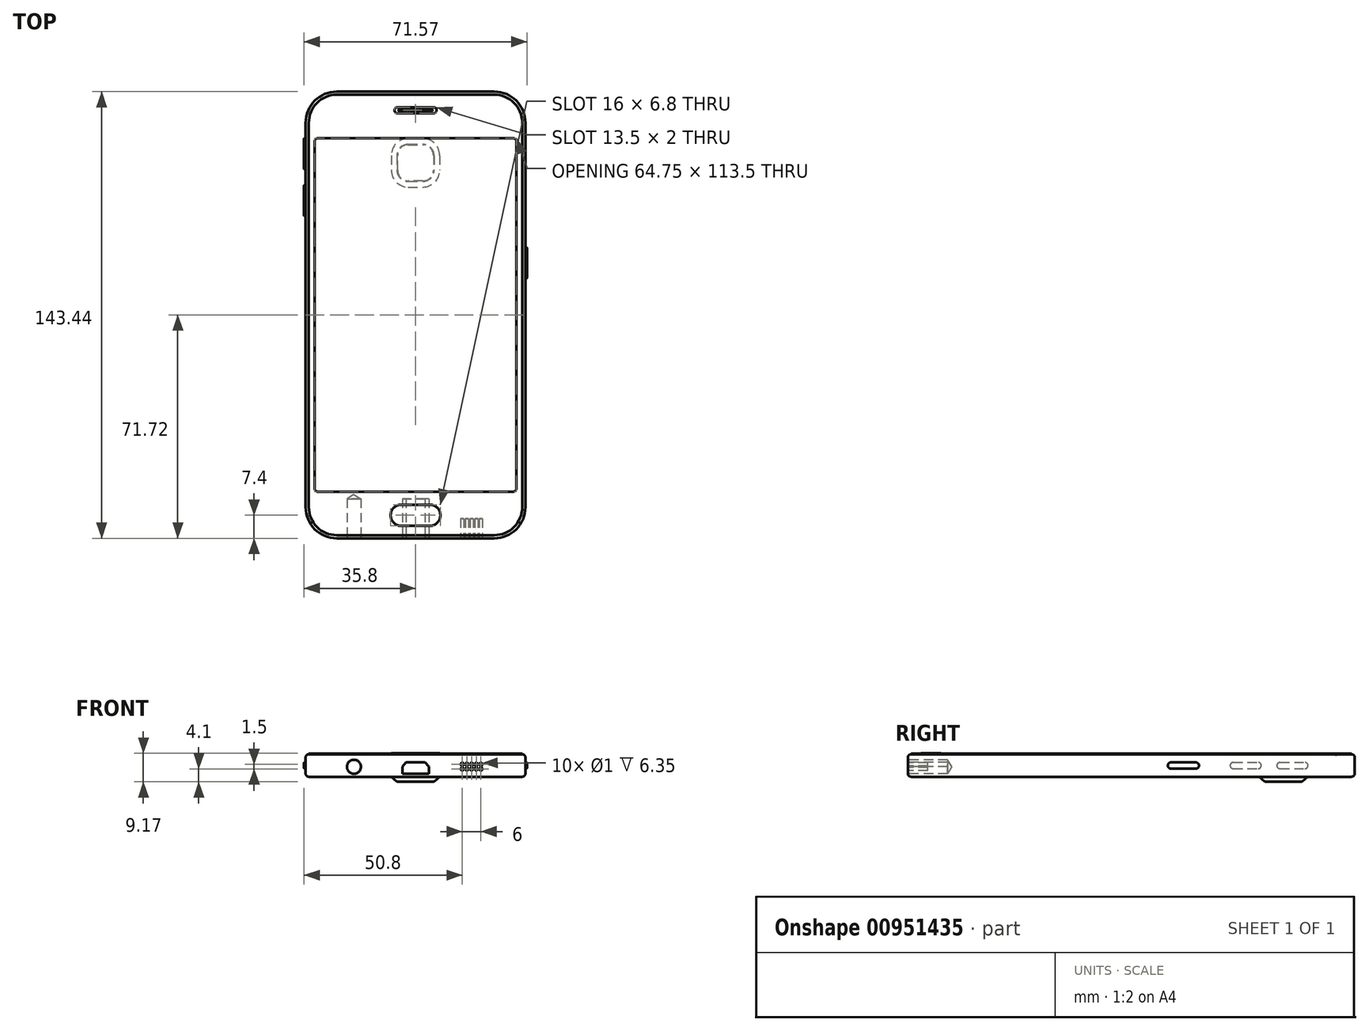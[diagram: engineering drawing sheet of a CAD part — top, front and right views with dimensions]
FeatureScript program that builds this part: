
annotation { "Feature Type Name" : "Feature", "Feature Type Description" : "" }
export const myFeature = defineFeature(function(context is Context, id is Id, definition is map)
    precondition{}
    {
        {
            var Q0;
            Q0=qCreatedBy(makeId("Top.planeOp"),FACE);
            var sketch = newSketch(context, id + "F0", { "sketchPlane" : qUnion([Q0])});
            skLineSegment(sketch, "E0.bottom", {"start": v(-35.27, 71.72) * mm, "end": v(35.27, 71.72) * mm});
            skLineSegment(sketch, "E0.top", {"start": v(-35.27, -71.72) * mm, "end": v(35.27, -71.72) * mm});
            skLineSegment(sketch, "E0.left", {"start": v(-35.27, 71.72) * mm, "end": v(-35.27, -71.72) * mm});
            skLineSegment(sketch, "E0.right", {"start": v(35.27, 71.72) * mm, "end": v(35.27, -71.72) * mm});
            skLineSegment(sketch, "E1", {"start": v(0, 0) * mm, "end": v(0, -71.72) * mm, "construction": true});
            skLineSegment(sketch, "E2", {"start": v(-35.27, 0) * mm, "end": v(0, 0) * mm, "construction": true});
            skPoint(sketch, "E3.orphan", {"position": v(35.27, 0) * mm});
            skPoint(sketch, "E4.orphan", {"position": v(0, 71.72) * mm});
            skSolve(sketch);
        }
        {
            var Q0;
            Q0=makeQuery(id+"F0.imprint","IMPRINT",FACE,{"disambiguationData":[TD([[makeQuery(id+"F0.imprint","IMPRINT",EDGE,{"derivedFrom":sQuery(id+"F0.wireOp",EDGE,"E0.bottom")}),-1.0]])]});
            extrude(context, id + "F1", {"entities" : qUnion([Q0]), "depth" : 7.22 * mm});
        }
        {
            var Q0;
            Q0=makeQuery(id+"F1.opExtrude","SWEPT_EDGE",EDGE,{"disambiguationData":[OSD([sQuery(id+"F0.wireOp",EDGE,"E0.bottom"),sQuery(id+"F0.wireOp",EDGE,"E0.left")])]});
            var Q1;
            Q1=makeQuery(id+"F1.opExtrude","SWEPT_EDGE",EDGE,{"disambiguationData":[OSD([sQuery(id+"F0.wireOp",EDGE,"E0.top"),sQuery(id+"F0.wireOp",EDGE,"E0.left")])]});
            var Q2;
            Q2=makeQuery(id+"F1.opExtrude","SWEPT_EDGE",EDGE,{"disambiguationData":[OSD([sQuery(id+"F0.wireOp",EDGE,"E0.top"),sQuery(id+"F0.wireOp",EDGE,"E0.right")])]});
            var Q3;
            Q3=makeQuery(id+"F1.opExtrude","SWEPT_EDGE",EDGE,{"disambiguationData":[OSD([sQuery(id+"F0.wireOp",EDGE,"E0.bottom"),sQuery(id+"F0.wireOp",EDGE,"E0.right")])]});
            fillet(context, id + "F2", {"entities" : qUnion([Q0, Q1, Q2, Q3]), "radius" : 10 * mm, "tangentPropagation" : true, "allowEdgeOverflow" : false});
        }
        {
            var Q0;
            Q0=makeQuery(id+"F1.opExtrude","CAP_FACE",FACE,{"disambiguationData":[OSD([sQuery(id+"F0.wireOp",EDGE,"E0.bottom"),sQuery(id+"F0.wireOp",EDGE,"E0.top"),sQuery(id+"F0.wireOp",EDGE,"E0.left"),sQuery(id+"F0.wireOp",EDGE,"E0.right")])],"isStart":false});
            var sketch = newSketch(context, id + "F3", { "sketchPlane" : qUnion([Q0])});
            skLineSegment(sketch, "E5.bottom", {"start": v(-4.6, -60.92) * mm, "end": v(4.6, -60.92) * mm});
            skLineSegment(sketch, "E5.top", {"start": v(-4.6, -67.72) * mm, "end": v(4.6, -67.72) * mm});
            skLineSegment(sketch, "E5.left", {"start": v(-8, -64.32) * mm, "end": v(-8, -64.32) * mm});
            skLineSegment(sketch, "E5.right", {"start": v(8, -64.32) * mm, "end": v(8, -64.32) * mm});
            skLineSegment(sketch, "E6", {"start": v(-8, -64.32) * mm, "end": v(8, -64.32) * mm, "construction": true});
            skLineSegment(sketch, "E7", {"start": v(0, -60.92) * mm, "end": v(0, -67.72) * mm, "construction": true});
            skPoint(sketch, "E8.visualSharp", {"position": v(-8, -60.92) * mm});
            skArc(sketch, "E8.filletArc", {"start": v(-4.6, -60.92) * mm, "mid": v(-7, -61.92) * mm, "end": v(-8, -64.32) * mm});
            skPoint(sketch, "E9.visualSharp", {"position": v(8, -60.92) * mm});
            skArc(sketch, "E9.filletArc", {"start": v(8, -64.32) * mm, "mid": v(7, -61.92) * mm, "end": v(4.6, -60.92) * mm});
            skPoint(sketch, "E10.visualSharp", {"position": v(8, -67.72) * mm});
            skArc(sketch, "E10.filletArc", {"start": v(4.6, -67.72) * mm, "mid": v(7, -66.72) * mm, "end": v(8, -64.32) * mm});
            skPoint(sketch, "E11.visualSharp", {"position": v(-8, -67.72) * mm});
            skArc(sketch, "E11.filletArc", {"start": v(-8, -64.32) * mm, "mid": v(-7, -66.72) * mm, "end": v(-4.6, -67.72) * mm});
            skSolve(sketch);
        }
        {
            var Q0;
            Q0=makeQuery(id+"F3.imprint","IMPRINT",FACE,{"disambiguationData":[TD([[makeQuery(id+"F3.imprint","IMPRINT",EDGE,{"derivedFrom":sQuery(id+"F3.wireOp",EDGE,"E5.bottom")}),-1.0]])]});
            extrude(context, id + "F4", {"entities" : qUnion([Q0]), "operationType" : NewBodyOperationType.ADD, "depth" : .35 * mm});
        }
        {
            var Q0;
            Q0=makeQuery(id+"F1.opExtrude","CAP_EDGE",EDGE,{"disambiguationData":[OSD([sQuery(id+"F0.wireOp",EDGE,"E0.left")])],"isStart":false});
            var Q1;
            Q1=makeQuery(id+"F1.opExtrude","CAP_EDGE",EDGE,{"disambiguationData":[OSD([sQuery(id+"F0.wireOp",EDGE,"E0.left")])],"isStart":true});
            fillet(context, id + "F5", {"entities" : qUnion([Q0, Q1]), "radius" : 1 * mm, "tangentPropagation" : true, "allowEdgeOverflow" : false});
        }
        {
            var Q0;
            Q0=makeQuery(id+"F1.opExtrude","SWEPT_FACE",FACE,{"disambiguationData":[OSD([sQuery(id+"F0.wireOp",EDGE,"E0.left")])]});
            var sketch = newSketch(context, id + "F6", { "sketchPlane" : qUnion([Q0])});
            skLineSegment(sketch, "E12.bottom", {"start": v(-31.72, 4.61) * mm, "end": v(-41.72, 4.61) * mm});
            skLineSegment(sketch, "E12.top", {"start": v(-31.72, 2.6) * mm, "end": v(-41.72, 2.61) * mm});
            skLineSegment(sketch, "E12.left", {"start": v(-31.72, 4.61) * mm, "end": v(-31.72, 2.6) * mm});
            skLineSegment(sketch, "E12.right", {"start": v(-41.72, 4.61) * mm, "end": v(-41.72, 2.61) * mm});
            skLineSegment(sketch, "E13.bottom", {"start": v(-46.72, 4.61) * mm, "end": v(-56.72, 4.61) * mm});
            skLineSegment(sketch, "E13.top", {"start": v(-46.72, 2.61) * mm, "end": v(-56.72, 2.61) * mm});
            skLineSegment(sketch, "E13.left", {"start": v(-46.72, 4.61) * mm, "end": v(-46.72, 2.61) * mm});
            skLineSegment(sketch, "E13.right", {"start": v(-56.72, 4.61) * mm, "end": v(-56.72, 2.61) * mm});
            skLineSegment(sketch, "E14", {"start": v(-31.72, 3.6) * mm, "end": v(-41.72, 3.6) * mm, "construction": true});
            skLineSegment(sketch, "E15", {"start": v(-36.72, 2.6) * mm, "end": v(-36.72, 4.6) * mm, "construction": true});
            skLineSegment(sketch, "E16", {"start": v(-51.72, 4.6) * mm, "end": v(-51.72, 2.61) * mm, "construction": true});
            skLineSegment(sketch, "E17", {"start": v(-46.72, 3.6) * mm, "end": v(-56.72, 3.6) * mm, "construction": true});
            skSolve(sketch);
        }
        {
            var Q0;
            Q0=qSketchRegion(id+"F6",true);
            extrude(context, id + "F7", {"entities" : qUnion([Q0]), "operationType" : NewBodyOperationType.ADD, "depth" : .53 * mm});
        }
        {
            var Q0;
            Q0=makeQuery(id+"F7.opExtrude","SWEPT_EDGE",EDGE,{"disambiguationData":[OSD([sQuery(id+"F6.wireOp",EDGE,"E13.bottom"),sQuery(id+"F6.wireOp",EDGE,"E13.right")])]});
            var Q1;
            Q1=makeQuery(id+"F7.opExtrude","SWEPT_EDGE",EDGE,{"disambiguationData":[OSD([sQuery(id+"F6.wireOp",EDGE,"E13.top"),sQuery(id+"F6.wireOp",EDGE,"E13.right")])]});
            var Q2;
            Q2=makeQuery(id+"F7.opExtrude","SWEPT_EDGE",EDGE,{"disambiguationData":[OSD([sQuery(id+"F6.wireOp",EDGE,"E13.top"),sQuery(id+"F6.wireOp",EDGE,"E13.left")])]});
            var Q3;
            Q3=makeQuery(id+"F7.opExtrude","SWEPT_EDGE",EDGE,{"disambiguationData":[OSD([sQuery(id+"F6.wireOp",EDGE,"E13.bottom"),sQuery(id+"F6.wireOp",EDGE,"E13.left")])]});
            var Q4;
            Q4=makeQuery(id+"F7.opExtrude","SWEPT_EDGE",EDGE,{"disambiguationData":[OSD([sQuery(id+"F6.wireOp",EDGE,"E12.bottom"),sQuery(id+"F6.wireOp",EDGE,"E12.right")])]});
            var Q5;
            Q5=makeQuery(id+"F7.opExtrude","SWEPT_EDGE",EDGE,{"disambiguationData":[OSD([sQuery(id+"F6.wireOp",EDGE,"E12.top"),sQuery(id+"F6.wireOp",EDGE,"E12.right")])]});
            var Q6;
            Q6=makeQuery(id+"F7.opExtrude","SWEPT_EDGE",EDGE,{"disambiguationData":[OSD([sQuery(id+"F6.wireOp",EDGE,"E12.top"),sQuery(id+"F6.wireOp",EDGE,"E12.left")])]});
            var Q7;
            Q7=makeQuery(id+"F7.opExtrude","SWEPT_EDGE",EDGE,{"disambiguationData":[OSD([sQuery(id+"F6.wireOp",EDGE,"E12.bottom"),sQuery(id+"F6.wireOp",EDGE,"E12.left")])]});
            fillet(context, id + "F8", {"entities" : qUnion([Q0, Q1, Q2, Q3, Q4, Q5, Q6, Q7]), "radius" : 1 * mm, "tangentPropagation" : true, "allowEdgeOverflow" : false});
        }
        {
            var Q0;
            Q0=makeQuery(id+"F7.opExtrude","CAP_EDGE",EDGE,{"disambiguationData":[OSD([sQuery(id+"F6.wireOp",EDGE,"E13.top")])],"isStart":false});
            var Q1;
            Q1=makeQuery(id+"F7.opExtrude","CAP_EDGE",EDGE,{"disambiguationData":[OSD([sQuery(id+"F6.wireOp",EDGE,"E12.top")])],"isStart":false});
            fillet(context, id + "F9", {"entities" : qUnion([Q0, Q1]), "radius" : .25 * mm, "tangentPropagation" : true, "allowEdgeOverflow" : false});
        }
        {
            var Q0;
            Q0=makeQuery(id+"F1.opExtrude","CAP_FACE",FACE,{"disambiguationData":[OSD([sQuery(id+"F0.wireOp",EDGE,"E0.bottom"),sQuery(id+"F0.wireOp",EDGE,"E0.top"),sQuery(id+"F0.wireOp",EDGE,"E0.left"),sQuery(id+"F0.wireOp",EDGE,"E0.right")])],"isStart":true});
            var sketch = newSketch(context, id + "F10", { "sketchPlane" : qUnion([Q0])});
            skLineSegment(sketch, "E18.bottom", {"start": v(7.88, -40.97) * mm, "end": v(-7.87, -40.97) * mm});
            skLineSegment(sketch, "E18.top", {"start": v(7.88, -56.72) * mm, "end": v(-7.87, -56.72) * mm});
            skLineSegment(sketch, "E18.left", {"start": v(7.88, -40.97) * mm, "end": v(7.88, -56.72) * mm});
            skLineSegment(sketch, "E18.right", {"start": v(-7.87, -40.97) * mm, "end": v(-7.87, -56.72) * mm});
            skLineSegment(sketch, "E19", {"start": v(0, -40.97) * mm, "end": v(0, -56.72) * mm, "construction": true});
            skLineSegment(sketch, "E20", {"start": v(-7.87, -48.84) * mm, "end": v(7.88, -48.84) * mm, "construction": true});
            skSolve(sketch);
        }
        {
            var Q0;
            Q0=qSketchRegion(id+"F10",true);
            extrude(context, id + "F11", {"entities" : qUnion([Q0]), "operationType" : NewBodyOperationType.ADD, "depth" : 1.6 * mm});
        }
        {
            var Q0;
            Q0=makeQuery(id+"F11.opExtrude","SWEPT_EDGE",EDGE,{"disambiguationData":[OSD([sQuery(id+"F10.wireOp",EDGE,"E18.bottom"),sQuery(id+"F10.wireOp",EDGE,"E18.right")])]});
            var Q1;
            Q1=makeQuery(id+"F11.opExtrude","SWEPT_EDGE",EDGE,{"disambiguationData":[OSD([sQuery(id+"F10.wireOp",EDGE,"E18.top"),sQuery(id+"F10.wireOp",EDGE,"E18.right")])]});
            var Q2;
            Q2=makeQuery(id+"F11.opExtrude","SWEPT_EDGE",EDGE,{"disambiguationData":[OSD([sQuery(id+"F10.wireOp",EDGE,"E18.top"),sQuery(id+"F10.wireOp",EDGE,"E18.left")])]});
            var Q3;
            Q3=makeQuery(id+"F11.opExtrude","SWEPT_EDGE",EDGE,{"disambiguationData":[OSD([sQuery(id+"F10.wireOp",EDGE,"E18.bottom"),sQuery(id+"F10.wireOp",EDGE,"E18.left")])]});
            fillet(context, id + "F12", {"entities" : qUnion([Q0, Q1, Q2, Q3]), "radius" : 5.5 * mm, "tangentPropagation" : true, "allowEdgeOverflow" : false});
        }
        {
            var Q0;
            Q0=makeQuery(id+"F11.opExtrude","CAP_EDGE",EDGE,{"disambiguationData":[OSD([sQuery(id+"F10.wireOp",EDGE,"E18.right")])],"isStart":false});
            chamfer(context, id + "F13", {"entities" : qUnion([Q0]), "chamferType" : ChamferType.OFFSET_ANGLE, "width" : 2 * mm, "oppositeDirection" : false, "angle" : 40 * degree, "tangentPropagation" : true});
        }
        {
            var Q0;
            {var subQ0=sQuery(id+"F10.wireOp",EDGE,"E18.right");var subQ1=sQuery(id+"F10.wireOp",EDGE,"E18.top");var subQ2=makeQuery(id+"F11.opExtrude","CAP_FACE",FACE,{"disambiguationData":[OSD([sQuery(id+"F10.wireOp",EDGE,"E18.bottom"),subQ1,sQuery(id+"F10.wireOp",EDGE,"E18.left"),subQ0])],"isStart":false});Q0=makeQuery(id+"F13.opChamfer","BLEND_EDGE",EDGE,{"blendedFrom":[makeQuery(id+"F12.opFillet","BLEND_EDGE",EDGE,{"blendedFrom":[makeQuery(id+"F11.opExtrude","SWEPT_EDGE",EDGE,{"disambiguationData":[OSD([subQ1,subQ0])]}),subQ2],"blendedInto":[subQ2]}),subQ2],"blendedInto":[subQ2]});}
            chamfer(context, id + "F14", {"entities" : qUnion([Q0]), "width" : .25 * mm, "tangentPropagation" : true});
        }
        {
            var Q0;
            Q0=makeQuery(id+"F4.opExtrude","CAP_EDGE",EDGE,{"disambiguationData":[OSD([sQuery(id+"F3.wireOp",EDGE,"E5.top")])],"isStart":false});
            fillet(context, id + "F15", {"entities" : qUnion([Q0]), "radius" : .5 * mm, "tangentPropagation" : true, "allowEdgeOverflow" : false});
        }
        {
            var Q0;
            Q0=makeQuery(id+"F1.opExtrude","SWEPT_FACE",FACE,{"disambiguationData":[OSD([sQuery(id+"F0.wireOp",EDGE,"E0.right")])]});
            var sketch = newSketch(context, id + "F16", { "sketchPlane" : qUnion([Q0])});
            skLineSegment(sketch, "E21.bottom", {"start": v(11.72, 4.61) * mm, "end": v(21.72, 4.61) * mm});
            skLineSegment(sketch, "E21.top", {"start": v(11.72, 2.61) * mm, "end": v(21.72, 2.61) * mm});
            skLineSegment(sketch, "E21.left", {"start": v(11.72, 4.61) * mm, "end": v(11.72, 2.61) * mm});
            skLineSegment(sketch, "E21.right", {"start": v(21.72, 4.61) * mm, "end": v(21.72, 2.61) * mm});
            skLineSegment(sketch, "E22", {"start": v(11.72, 3.6) * mm, "end": v(21.72, 3.6) * mm, "construction": true});
            skLineSegment(sketch, "E23", {"start": v(16.72, 2.61) * mm, "end": v(16.72, 4.61) * mm, "construction": true});
            skSolve(sketch);
        }
        {
            var Q0;
            Q0=makeQuery(id+"F16.imprint","IMPRINT",FACE,{"disambiguationData":[TD([[makeQuery(id+"F16.imprint","IMPRINT",EDGE,{"derivedFrom":sQuery(id+"F16.wireOp",EDGE,"E21.bottom")}),-1.0]])]});
            extrude(context, id + "F17", {"entities" : qUnion([Q0]), "operationType" : NewBodyOperationType.ADD, "depth" : .5 * mm});
        }
        {
            var Q0;
            Q0=makeQuery(id+"F17.opExtrude","SWEPT_EDGE",EDGE,{"disambiguationData":[OSD([sQuery(id+"F16.wireOp",EDGE,"E21.bottom"),sQuery(id+"F16.wireOp",EDGE,"E21.left")])]});
            var Q1;
            Q1=makeQuery(id+"F17.opExtrude","SWEPT_EDGE",EDGE,{"disambiguationData":[OSD([sQuery(id+"F16.wireOp",EDGE,"E21.top"),sQuery(id+"F16.wireOp",EDGE,"E21.left")])]});
            var Q2;
            Q2=makeQuery(id+"F17.opExtrude","SWEPT_EDGE",EDGE,{"disambiguationData":[OSD([sQuery(id+"F16.wireOp",EDGE,"E21.top"),sQuery(id+"F16.wireOp",EDGE,"E21.right")])]});
            var Q3;
            Q3=makeQuery(id+"F17.opExtrude","SWEPT_EDGE",EDGE,{"disambiguationData":[OSD([sQuery(id+"F16.wireOp",EDGE,"E21.bottom"),sQuery(id+"F16.wireOp",EDGE,"E21.right")])]});
            fillet(context, id + "F18", {"entities" : qUnion([Q0, Q1, Q2, Q3]), "radius" : 1 * mm, "tangentPropagation" : true, "allowEdgeOverflow" : false});
        }
        {
            var Q0;
            Q0=makeQuery(id+"F17.opExtrude","CAP_EDGE",EDGE,{"disambiguationData":[OSD([sQuery(id+"F16.wireOp",EDGE,"E21.bottom")])],"isStart":false});
            fillet(context, id + "F19", {"entities" : qUnion([Q0]), "radius" : .25 * mm, "tangentPropagation" : true, "allowEdgeOverflow" : false});
        }
        {
            var Q0;
            Q0=makeQuery(id+"F1.opExtrude","SWEPT_FACE",FACE,{"disambiguationData":[OSD([sQuery(id+"F0.wireOp",EDGE,"E0.top")])]});
            var sketch = newSketch(context, id + "F20", { "sketchPlane" : qUnion([Q0])});
            skCircle(sketch, "E24", {"center": v(-19.77, 3.2) * mm, "radius": 2.25 * mm});
            skSolve(sketch);
        }
        {
            var Q0;
            Q0=sQuery(id+"F20.wireOp",VERTEX,"E24.center");
            var Q1;
            Q1=makeQuery(id+"F1.opExtrude","SWEPT_BODY",BODY,{"disambiguationData":[OSD([sQuery(id+"F0.wireOp",EDGE,"E0.bottom"),sQuery(id+"F0.wireOp",EDGE,"E0.top"),sQuery(id+"F0.wireOp",EDGE,"E0.left"),sQuery(id+"F0.wireOp",EDGE,"E0.right")])]});
            hole(context, id + "F21", {"style" : HoleStyle.SIMPLE, "endStyle" : HoleEndStyle.BLIND, "holeDiameter" : 4.5 * mm, "holeDepth" : 12.7 * mm, "tappedDepth" : 12.7 * mm, "tapClearance" : 3, "locations" : qUnion([Q0]), "scope" : qUnion([Q1])});
        }
        {
            var Q0;
            Q0=makeQuery(id+"F1.opExtrude","SWEPT_FACE",FACE,{"disambiguationData":[OSD([sQuery(id+"F0.wireOp",EDGE,"E0.top")])]});
            var sketch = newSketch(context, id + "F22", { "sketchPlane" : qUnion([Q0])});
            skLineSegment(sketch, "E25", {"start": v(-4.25, 3.3) * mm, "end": v(-4.25, 1) * mm});
            skLineSegment(sketch, "E26", {"start": v(-4.25, 1) * mm, "end": v(4.25, 1) * mm});
            skLineSegment(sketch, "E27", {"start": v(4.25, 1) * mm, "end": v(4.25, 3.3) * mm});
            skLineSegment(sketch, "E28", {"start": v(4.25, 3.3) * mm, "end": v(3, 4.6) * mm});
            skLineSegment(sketch, "E29", {"start": v(3, 4.6) * mm, "end": v(-3, 4.6) * mm});
            skLineSegment(sketch, "E30", {"start": v(-3, 4.6) * mm, "end": v(-4.25, 3.3) * mm});
            skLineSegment(sketch, "E31", {"start": v(0, 4.6) * mm, "end": v(0, 1) * mm, "construction": true});
            skSolve(sketch);
        }
        {
            var Q0;
            Q0=makeQuery(id+"F22.imprint","IMPRINT",FACE,{"disambiguationData":[TD([[makeQuery(id+"F22.imprint","IMPRINT",EDGE,{"derivedFrom":sQuery(id+"F22.wireOp",EDGE,"E25")}),1.0]])]});
            extrude(context, id + "F23", {"entities" : qUnion([Q0]), "operationType" : NewBodyOperationType.REMOVE, "oppositeDirection" : true, "depth" : 12.7 * mm});
        }
        {
            var Q0;
            Q0=makeQuery(id+"F1.opExtrude","SWEPT_FACE",FACE,{"disambiguationData":[OSD([sQuery(id+"F0.wireOp",EDGE,"E0.top")])]});
            var sketch = newSketch(context, id + "F24", { "sketchPlane" : qUnion([Q0])});
            skCircle(sketch, "E32", {"center": v(15, 2.5) * mm, "radius": 0.5 * mm});
            skCircle(sketch, "E33.0.1.0", {"center": v(15, 4) * mm, "radius": 0.5 * mm});
            skCircle(sketch, "E33.1.0.0", {"center": v(16.5, 2.5) * mm, "radius": 0.5 * mm});
            skCircle(sketch, "E33.1.1.0", {"center": v(16.5, 4) * mm, "radius": 0.5 * mm});
            skCircle(sketch, "E33.2.0.0", {"center": v(18, 2.5) * mm, "radius": 0.5 * mm});
            skCircle(sketch, "E33.2.1.0", {"center": v(18, 4) * mm, "radius": 0.5 * mm});
            skCircle(sketch, "E33.3.0.0", {"center": v(19.5, 2.5) * mm, "radius": 0.5 * mm});
            skCircle(sketch, "E33.3.1.0", {"center": v(19.5, 4) * mm, "radius": 0.5 * mm});
            skCircle(sketch, "E33.4.0.0", {"center": v(21, 2.5) * mm, "radius": 0.5 * mm});
            skCircle(sketch, "E33.4.1.0", {"center": v(21, 4) * mm, "radius": 0.5 * mm});
            skLineSegment(sketch, "E33.direction1", {"start": v(15, 2.5) * mm, "end": v(16.5, 2.5) * mm, "construction": true});
            skLineSegment(sketch, "E33.direction2", {"start": v(15, 2.5) * mm, "end": v(15, 4) * mm, "construction": true});
            skSolve(sketch);
        }
        {
            var Q0;
            Q0=qSketchRegion(id+"F24",true);
            extrude(context, id + "F25", {"entities" : qUnion([Q0]), "operationType" : NewBodyOperationType.REMOVE, "oppositeDirection" : true, "depth" : 6.35 * mm});
        }
        {
            var Q0;
            Q0=makeQuery(id+"F1.opExtrude","CAP_FACE",FACE,{"disambiguationData":[OSD([sQuery(id+"F0.wireOp",EDGE,"E0.bottom"),sQuery(id+"F0.wireOp",EDGE,"E0.top"),sQuery(id+"F0.wireOp",EDGE,"E0.left"),sQuery(id+"F0.wireOp",EDGE,"E0.right")])],"isStart":false});
            var sketch = newSketch(context, id + "F26", { "sketchPlane" : qUnion([Q0])});
            skCircle(sketch, "E34", {"center": v(-5.25, 65.72) * mm, "radius": 0.25 * mm});
            skCircle(sketch, "E35.1.0.0", {"center": v(-4.5, 65.72) * mm, "radius": 0.25 * mm});
            skCircle(sketch, "E35.2.0.0", {"center": v(-3.75, 65.72) * mm, "radius": 0.25 * mm});
            skCircle(sketch, "E35.3.0.0", {"center": v(-3, 65.72) * mm, "radius": 0.25 * mm});
            skCircle(sketch, "E35.4.0.0", {"center": v(-2.25, 65.72) * mm, "radius": 0.25 * mm});
            skCircle(sketch, "E35.5.0.0", {"center": v(-1.5, 65.72) * mm, "radius": 0.25 * mm});
            skCircle(sketch, "E35.6.0.0", {"center": v(-0.75, 65.72) * mm, "radius": 0.25 * mm});
            skCircle(sketch, "E35.7.0.0", {"center": v(0, 65.72) * mm, "radius": 0.25 * mm});
            skCircle(sketch, "E35.8.0.0", {"center": v(0.75, 65.72) * mm, "radius": 0.25 * mm});
            skCircle(sketch, "E35.9.0.0", {"center": v(1.5, 65.72) * mm, "radius": 0.25 * mm});
            skCircle(sketch, "E35.10.0.0", {"center": v(2.25, 65.72) * mm, "radius": 0.25 * mm});
            skCircle(sketch, "E35.11.0.0", {"center": v(3, 65.72) * mm, "radius": 0.25 * mm});
            skCircle(sketch, "E35.12.0.0", {"center": v(3.75, 65.72) * mm, "radius": 0.25 * mm});
            skCircle(sketch, "E35.13.0.0", {"center": v(4.5, 65.72) * mm, "radius": 0.25 * mm});
            skCircle(sketch, "E35.14.0.0", {"center": v(5.25, 65.72) * mm, "radius": 0.25 * mm});
            skLineSegment(sketch, "E35.direction1", {"start": v(-5.25, 65.72) * mm, "end": v(-4.5, 65.72) * mm, "construction": true});
            skLineSegment(sketch, "E36", {"start": v(0, 65.72) * mm, "end": v(0, 65.97) * mm, "construction": true});
            skSolve(sketch);
        }
        {
            var Q0;
            Q0=qSketchRegion(id+"F26",true);
            extrude(context, id + "F27", {"entities" : qUnion([Q0]), "operationType" : NewBodyOperationType.REMOVE, "oppositeDirection" : true, "depth" : .25 * mm});
        }
        {
            var Q0;
            Q0=makeQuery(id+"F1.opExtrude","CAP_FACE",FACE,{"disambiguationData":[OSD([sQuery(id+"F0.wireOp",EDGE,"E0.bottom"),sQuery(id+"F0.wireOp",EDGE,"E0.top"),sQuery(id+"F0.wireOp",EDGE,"E0.left"),sQuery(id+"F0.wireOp",EDGE,"E0.right")])],"isStart":false});
            var sketch = newSketch(context, id + "F28", { "sketchPlane" : qUnion([Q0])});
            skLineSegment(sketch, "E37.bottom", {"start": v(-6.75, 66.72) * mm, "end": v(6.75, 66.72) * mm});
            skLineSegment(sketch, "E37.top", {"start": v(-6.75, 64.72) * mm, "end": v(6.75, 64.72) * mm});
            skLineSegment(sketch, "E37.left", {"start": v(-6.75, 66.72) * mm, "end": v(-6.75, 64.72) * mm});
            skLineSegment(sketch, "E37.right", {"start": v(6.75, 66.72) * mm, "end": v(6.75, 64.72) * mm});
            skLineSegment(sketch, "E38", {"start": v(0, 64.72) * mm, "end": v(0, 66.72) * mm, "construction": true});
            skLineSegment(sketch, "E39", {"start": v(-6.75, 65.72) * mm, "end": v(6.75, 65.72) * mm, "construction": true});
            skLineSegment(sketch, "E40", {"start": v(0, 65.97) * mm, "end": v(0, 65.47) * mm, "construction": true});
            skLineSegment(sketch, "E41", {"start": v(0, 65.72) * mm, "end": v(0.25, 65.72) * mm, "construction": true});
            skSolve(sketch);
        }
        {
            var Q0;
            Q0=qSketchRegion(id+"F28",true);
            extrude(context, id + "F29", {"entities" : qUnion([Q0]), "operationType" : NewBodyOperationType.REMOVE, "oppositeDirection" : true, "depth" : .1 * mm});
        }
        {
            var Q0;
            Q0=makeQuery(id+"F29.boolean.opBoolean","COPY",EDGE,{"derivedFrom":makeQuery(id+"F29.opExtrude","SWEPT_EDGE",EDGE,{"disambiguationData":[OSD([sQuery(id+"F28.wireOp",EDGE,"E37.bottom"),sQuery(id+"F28.wireOp",EDGE,"E37.left")])]})});
            var Q1;
            Q1=makeQuery(id+"F29.boolean.opBoolean","COPY",EDGE,{"derivedFrom":makeQuery(id+"F29.opExtrude","SWEPT_EDGE",EDGE,{"disambiguationData":[OSD([sQuery(id+"F28.wireOp",EDGE,"E37.top"),sQuery(id+"F28.wireOp",EDGE,"E37.left")])]})});
            var Q2;
            Q2=makeQuery(id+"F29.boolean.opBoolean","COPY",EDGE,{"derivedFrom":makeQuery(id+"F29.opExtrude","SWEPT_EDGE",EDGE,{"disambiguationData":[OSD([sQuery(id+"F28.wireOp",EDGE,"E37.bottom"),sQuery(id+"F28.wireOp",EDGE,"E37.right")])]})});
            var Q3;
            Q3=makeQuery(id+"F29.boolean.opBoolean","COPY",EDGE,{"derivedFrom":makeQuery(id+"F29.opExtrude","SWEPT_EDGE",EDGE,{"disambiguationData":[OSD([sQuery(id+"F28.wireOp",EDGE,"E37.top"),sQuery(id+"F28.wireOp",EDGE,"E37.right")])]})});
            fillet(context, id + "F30", {"entities" : qUnion([Q0, Q1, Q2, Q3]), "radius" : 1 * mm, "tangentPropagation" : true, "allowEdgeOverflow" : false});
        }
        {
            var Q0;
            Q0=makeQuery(id+"F1.opExtrude","CAP_FACE",FACE,{"disambiguationData":[OSD([sQuery(id+"F0.wireOp",EDGE,"E0.bottom"),sQuery(id+"F0.wireOp",EDGE,"E0.top"),sQuery(id+"F0.wireOp",EDGE,"E0.left"),sQuery(id+"F0.wireOp",EDGE,"E0.right")])],"isStart":false});
            var sketch = newSketch(context, id + "F31", { "sketchPlane" : qUnion([Q0])});
            skLineSegment(sketch, "E42.bottom", {"start": v(-31.38, 56.75) * mm, "end": v(31.37, 56.75) * mm});
            skLineSegment(sketch, "E42.top", {"start": v(-31.38, -56.75) * mm, "end": v(31.38, -56.75) * mm});
            skLineSegment(sketch, "E42.left", {"start": v(-32.38, 55.75) * mm, "end": v(-32.38, -55.75) * mm});
            skLineSegment(sketch, "E42.right", {"start": v(32.37, 55.75) * mm, "end": v(32.37, -55.75) * mm});
            skLineSegment(sketch, "E43", {"start": v(0, 56.75) * mm, "end": v(0, -56.75) * mm, "construction": true});
            skPoint(sketch, "E43.endSnap0", {"position": v(0, -60.92) * mm});
            skLineSegment(sketch, "E44", {"start": v(-32.38, 0) * mm, "end": v(32.38, 0) * mm, "construction": true});
            skPoint(sketch, "E44.endSnap0", {"position": v(32.38, 0) * mm});
            skPoint(sketch, "E45.visualSharp", {"position": v(-32.38, 56.75) * mm});
            skArc(sketch, "E45.filletArc", {"start": v(-31.38, 56.75) * mm, "mid": v(-32.08, 56.46) * mm, "end": v(-32.38, 55.75) * mm});
            skPoint(sketch, "E46.visualSharp", {"position": v(32.37, 56.75) * mm});
            skArc(sketch, "E46.filletArc", {"start": v(32.38, 55.75) * mm, "mid": v(32.08, 56.46) * mm, "end": v(31.37, 56.75) * mm});
            skPoint(sketch, "E47.visualSharp", {"position": v(32.38, -56.75) * mm});
            skArc(sketch, "E47.filletArc", {"start": v(31.38, -56.75) * mm, "mid": v(32.08, -56.46) * mm, "end": v(32.38, -55.75) * mm});
            skPoint(sketch, "E48.visualSharp", {"position": v(-32.38, -56.75) * mm});
            skArc(sketch, "E48.filletArc", {"start": v(-32.38, -55.75) * mm, "mid": v(-32.08, -56.46) * mm, "end": v(-31.38, -56.75) * mm});
            skSolve(sketch);
        }
        {
            var Q0;
            Q0=makeQuery(id+"F31.imprint","IMPRINT",FACE,{"disambiguationData":[TD([[makeQuery(id+"F31.imprint","IMPRINT",EDGE,{"derivedFrom":sQuery(id+"F31.wireOp",EDGE,"E42.bottom")}),-1.0]])]});
            extrude(context, id + "F32", {"entities" : qUnion([Q0]), "operationType" : NewBodyOperationType.REMOVE, "oppositeDirection" : true, "depth" : .1 * mm});
        }
        {
            var Q0;
            Q0=makeQuery(id+"F32.boolean.opBoolean","COPY",FACE,{"derivedFrom":makeQuery(id+"F32.opExtrude","CAP_FACE",FACE,{"disambiguationData":[OSD([sQuery(id+"F31.wireOp",EDGE,"E42.bottom"),sQuery(id+"F31.wireOp",EDGE,"E42.top"),sQuery(id+"F31.wireOp",EDGE,"E42.left"),sQuery(id+"F31.wireOp",EDGE,"E42.right"),sQuery(id+"F31.wireOp",EDGE,"E45.filletArc"),sQuery(id+"F31.wireOp",EDGE,"E46.filletArc"),sQuery(id+"F31.wireOp",EDGE,"E47.filletArc"),sQuery(id+"F31.wireOp",EDGE,"E48.filletArc")])],"isStart":false})});
            extrude(context, id + "F33", {"entities" : qUnion([Q0]), "depth" : 0.2 * mm, "offsetDistance" : 25 * mm});
        }
        {
            var Q0;
            Q0=makeQuery(id+"F1.opExtrude","CAP_FACE",FACE,{"disambiguationData":[OSD([sQuery(id+"F0.wireOp",EDGE,"E0.bottom"),sQuery(id+"F0.wireOp",EDGE,"E0.top"),sQuery(id+"F0.wireOp",EDGE,"E0.left"),sQuery(id+"F0.wireOp",EDGE,"E0.right")])],"isStart":false});
            extrude(context, id + "F34", {"entities" : qUnion([Q0]), "depth" : 0.2 * mm, "offsetDistance" : 25 * mm});
        }
    });
